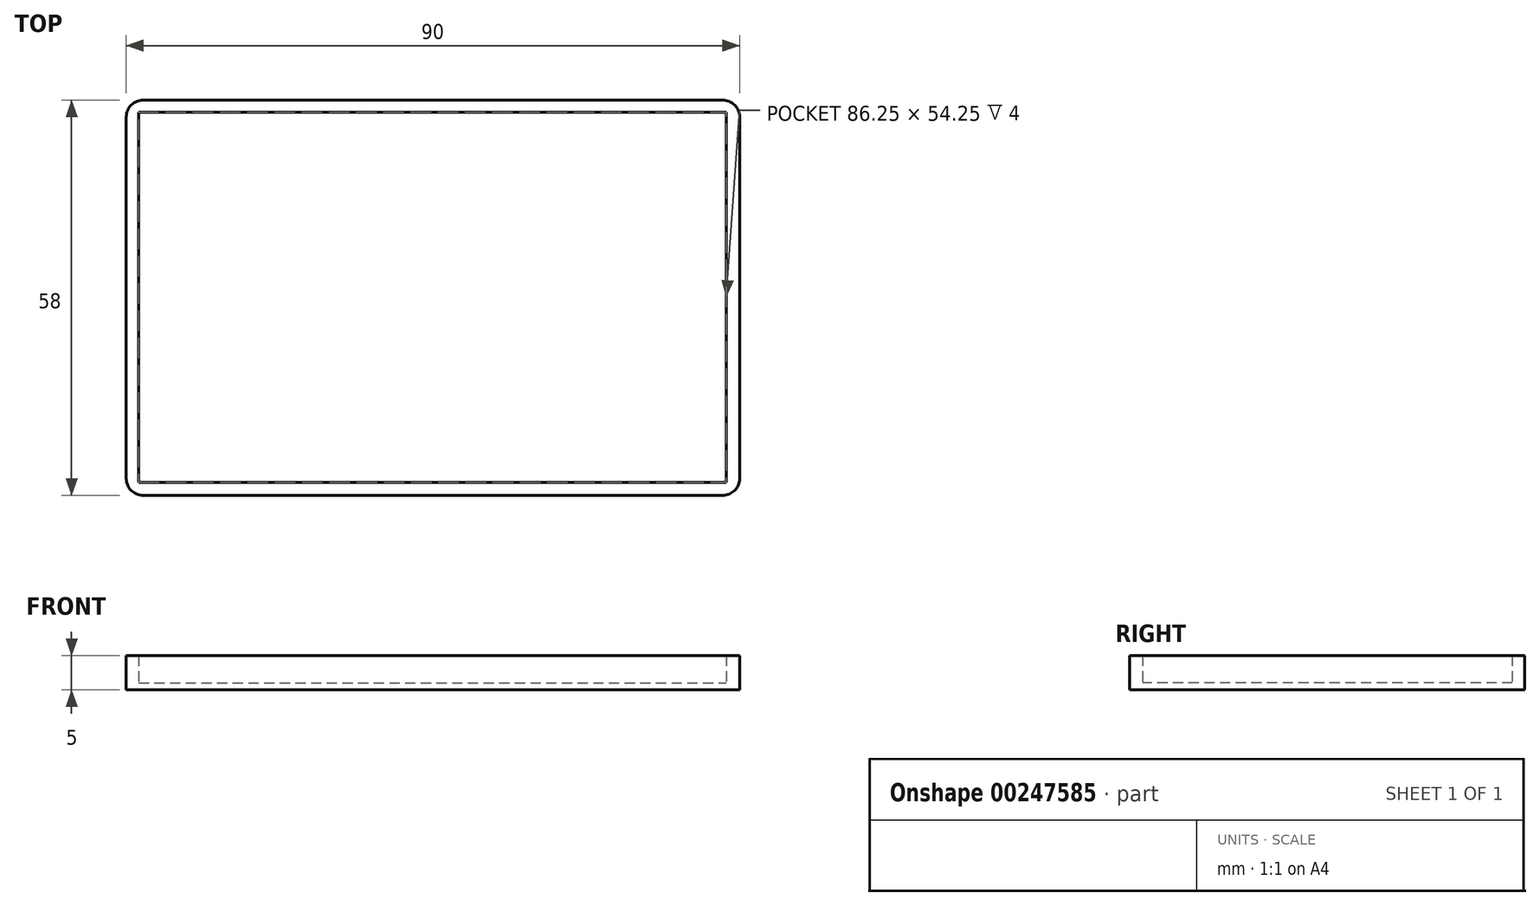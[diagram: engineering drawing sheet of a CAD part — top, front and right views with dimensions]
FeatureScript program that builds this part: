
annotation { "Feature Type Name" : "Feature", "Feature Type Description" : "" }
export const myFeature = defineFeature(function(context is Context, id is Id, definition is map)
    precondition{}
    {
        {
            var Q0;
            Q0=qCreatedBy(makeId("Top.planeOp"),FACE);
            var sketch = newSketch(context, id + "F0", { "sketchPlane" : qUnion([Q0])});
            skLineSegment(sketch, "E0.bottom", {"start": v(-40.9, -26.6) * mm, "end": v(44.1, -26.6) * mm});
            skLineSegment(sketch, "E0.top", {"start": v(-40.9, 31.4) * mm, "end": v(44.1, 31.4) * mm});
            skLineSegment(sketch, "E0.left", {"start": v(-43.4, -24.1) * mm, "end": v(-43.4, 28.9) * mm});
            skLineSegment(sketch, "E0.right", {"start": v(46.6, -24.1) * mm, "end": v(46.6, 28.9) * mm});
            skPoint(sketch, "E1.visualSharp", {"position": v(-43.4, 31.4) * mm});
            skArc(sketch, "E1.filletArc", {"start": v(-40.9, 31.4) * mm, "mid": v(-42.67, 30.67) * mm, "end": v(-43.4, 28.9) * mm});
            skPoint(sketch, "E2.visualSharp", {"position": v(46.6, 31.4) * mm});
            skArc(sketch, "E2.filletArc", {"start": v(46.6, 28.9) * mm, "mid": v(45.86, 30.67) * mm, "end": v(44.1, 31.4) * mm});
            skPoint(sketch, "E3.visualSharp", {"position": v(46.6, -26.6) * mm});
            skArc(sketch, "E3.filletArc", {"start": v(44.1, -26.6) * mm, "mid": v(45.86, -25.87) * mm, "end": v(46.6, -24.1) * mm});
            skPoint(sketch, "E4.visualSharp", {"position": v(-43.4, -26.6) * mm});
            skArc(sketch, "E4.filletArc", {"start": v(-43.4, -24.1) * mm, "mid": v(-42.67, -25.87) * mm, "end": v(-40.9, -26.6) * mm});
            skLineSegment(sketch, "E5.bottom", {"start": v(-41.59, 29.59) * mm, "end": v(44.66, 29.59) * mm});
            skLineSegment(sketch, "E5.top", {"start": v(-41.59, -24.66) * mm, "end": v(44.66, -24.66) * mm});
            skLineSegment(sketch, "E5.left", {"start": v(-41.59, 29.59) * mm, "end": v(-41.59, -24.66) * mm});
            skLineSegment(sketch, "E5.right", {"start": v(44.66, 29.59) * mm, "end": v(44.66, -24.66) * mm});
            skSolve(sketch);
        }
        {
            var Q0;
            Q0=makeQuery(id+"F0.imprint","IMPRINT",FACE,{"disambiguationData":[TD([[makeQuery(id+"F0.imprint","IMPRINT",EDGE,{"derivedFrom":sQuery(id+"F0.wireOp",EDGE,"E0.bottom")}),1.0]])]});
            extrude(context, id + "F1", {"entities" : qUnion([Q0]), "depth" : 5 * mm, "offsetDistance" : 25 * mm});
        }
        {
            var Q0;
            Q0=makeQuery(id+"F0.imprint","IMPRINT",FACE,{"disambiguationData":[TD([[makeQuery(id+"F0.imprint","IMPRINT",EDGE,{"derivedFrom":sQuery(id+"F0.wireOp",EDGE,"E5.bottom")}),-1.0]])]});
            extrude(context, id + "F2", {"entities" : qUnion([Q0]), "operationType" : NewBodyOperationType.ADD, "depth" : 1 * mm, "offsetDistance" : 25 * mm});
        }
    });
